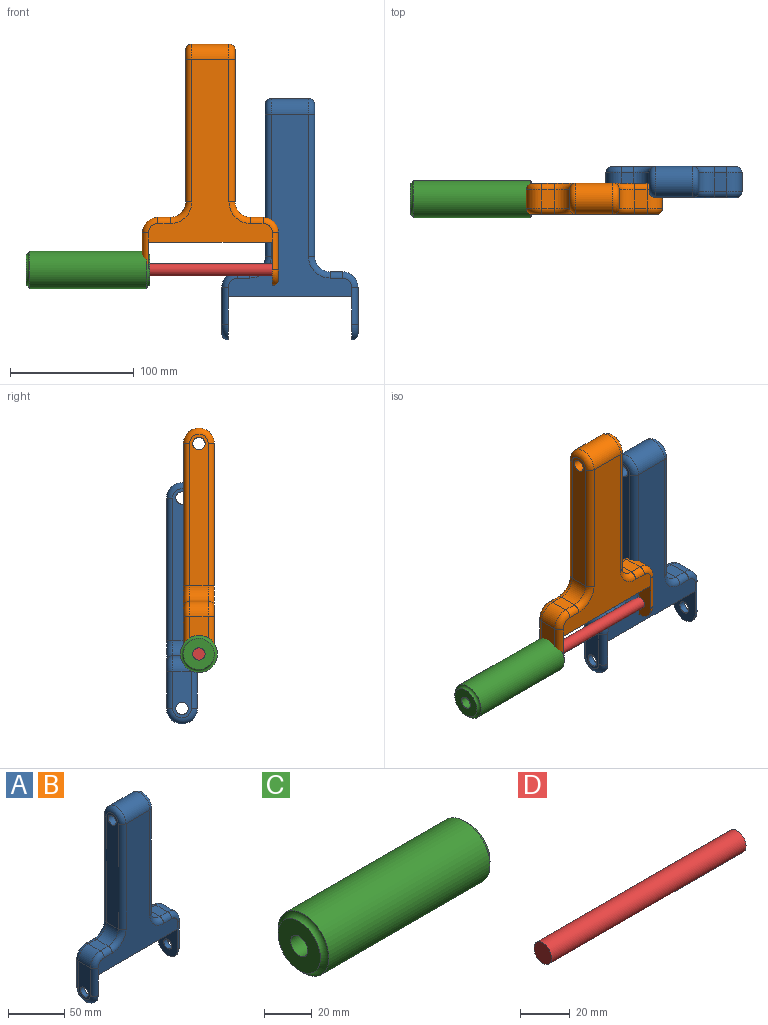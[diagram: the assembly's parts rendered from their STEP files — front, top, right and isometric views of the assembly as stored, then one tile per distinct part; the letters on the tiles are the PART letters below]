
ASSEMBLY  parts=4 mates=2
PART A: 43 faces, bbox 112.1x27.1x197.1 mm
  f0: plane 122.5x15mm, normal (-1,0,0), area 1734.8mm2, adj f11,f28,f29,f31,f42
  f1: plane 15x10mm, normal (0,0,1), area 150mm2, adj f11,f14,f32,f35
  f2: plane 37.5x15mm, normal (-1,0,0), area 459.8mm2, adj f14,f36,f38,f39,f41
  f3: plane 35x25mm, normal (1,0,0), area 729.4mm2, adj f4,f36,f38,f39,f41
  f4: plane 100x25mm, normal (0,0,-1), area 2500mm2, adj f3,f5,f9,f10
  f5: plane 35x25mm, normal (-1,0,0), area 729.4mm2, adj f4,f24,f26,f27,f40
  f6: plane 37.5x15mm, normal (1,0,0), area 459.8mm2, adj f13,f24,f26,f27,f40
  f7: plane 15x10mm, normal (0,0,1), area 150mm2, adj f12,f13,f20,f23
  f8: plane 122.5x15mm, normal (1,0,0), area 1734.8mm2, adj f12,f16,f17,f19,f42
  f9: plane 147.5x100mm, normal (0,-1,0), area 5582.3mm2, adj f4,f15,f19,f21,f23,f25,f27,f31
  f10: plane 147.5x100mm, normal (0,1,0), area 5582.3mm2, adj f4,f15,f16,f18,f20,f22,f24,f28
  f11: cylinder r=12.5mm len=15mm, axis (0,1,0), area 294.5mm2, adj f0,f1,f30,f33
  f12: cylinder r=12.5mm len=15mm, axis (0,-1,0), area 294.5mm2, adj f7,f8,f18,f21
  f13: cylinder r=12.5mm len=15mm, axis (0,1,0), area 294.5mm2, adj f6,f7,f22,f25
  f14: cylinder r=12.5mm len=15mm, axis (0,-1,0), area 294.5mm2, adj f1,f2,f34,f37
  f15: cylinder r=12.5mm len=30mm, axis (1,0,0), area 1178.1mm2, adj f9,f10,f17,f29
  f16: cylinder r=5mm len=115mm, axis (0,0,1), area 903.2mm2, adj f8,f10,f17,f18
  f17: torus R=7.5mm, axis (1,0,0), area 263.6mm2, adj f8,f15,f16,f19
  f18: torus R=17.5mm, axis (0,-1,0), area 176.6mm2, adj f10,f12,f16,f20
  f19: cylinder r=5mm len=115mm, axis (0,0,-1), area 903.2mm2, adj f8,f9,f17,f21
  f20: cylinder r=5mm len=10mm, axis (-1,0,0), area 78.5mm2, adj f7,f10,f18,f22
  f21: torus R=17.5mm, axis (0,-1,0), area 176.6mm2, adj f9,f12,f19,f23
  f22: torus R=7.5mm, axis (0,-1,0), area 131.8mm2, adj f10,f13,f20,f24
  f23: cylinder r=5mm len=10mm, axis (1,0,0), area 78.5mm2, adj f7,f9,f21,f25
  f24: cylinder r=5mm len=30mm, axis (0,0,1), area 235.6mm2, adj f5,f6,f10,f22,f26
  f25: torus R=7.5mm, axis (0,-1,0), area 131.8mm2, adj f9,f13,f23,f27
  f26: torus R=7.5mm, axis (1,0,0), area 263.6mm2, adj f5,f6,f24,f27
  f27: cylinder r=5mm len=30mm, axis (0,0,-1), area 235.6mm2, adj f5,f6,f9,f25,f26
  f28: cylinder r=5mm len=115mm, axis (0,0,-1), area 903.2mm2, adj f0,f10,f29,f30
  f29: torus R=7.5mm, axis (1,0,0), area 263.6mm2, adj f0,f15,f28,f31
  f30: torus R=17.5mm, axis (0,-1,0), area 176.6mm2, adj f10,f11,f28,f32
  f31: cylinder r=5mm len=115mm, axis (0,0,1), area 903.2mm2, adj f0,f9,f29,f33
  f32: cylinder r=5mm len=10mm, axis (-1,0,0), area 78.5mm2, adj f1,f10,f30,f34
  f33: torus R=17.5mm, axis (0,-1,0), area 176.6mm2, adj f9,f11,f31,f35
  f34: torus R=7.5mm, axis (0,-1,0), area 131.8mm2, adj f10,f14,f32,f36
  f35: cylinder r=5mm len=10mm, axis (1,0,0), area 78.5mm2, adj f1,f9,f33,f37
  f36: cylinder r=5mm len=30mm, axis (0,0,-1), area 235.6mm2, adj f2,f3,f10,f34,f38
  f37: torus R=7.5mm, axis (0,-1,0), area 131.8mm2, adj f9,f14,f35,f39
  f38: torus R=7.5mm, axis (1,0,0), area 263.6mm2, adj f2,f3,f36,f39
  f39: cylinder r=5mm len=30mm, axis (0,0,1), area 235.6mm2, adj f2,f3,f9,f37,f38
  f40: cylinder r=5mm len=10mm, axis (1,0,0), area 157.1mm2, adj f5,f6
  f41: cylinder r=5mm len=10mm, axis (1,0,0), area 157.1mm2, adj f2,f3
  f42: cylinder r=5mm len=40mm, axis (-1,0,0), area 1256.6mm2, adj f0,f8
PART B: same geometry as A
PART C: 6 faces, bbox 101.8x36.3x36.3 mm
  f0: plane 25x25mm, normal (1,0,0), area 412.3mm2, adj f1,f5
  f1: torus R=15mm, axis (-1,0,0), area 330.8mm2, adj f0,f2
  f2: cylinder r=15mm len=95mm, axis (-1,0,0), area 8953.5mm2, adj f1,f3
  f3: torus R=15mm, axis (-1,0,0), area 330.8mm2, adj f2,f4
  f4: plane 25x25mm, normal (-1,0,0), area 412.3mm2, adj f3,f5
  f5: cylinder r=5mm len=100mm, axis (1,0,0), area 3141.6mm2, adj f0,f4
PART D: 3 faces, bbox 110x10x10 mm
  f0: cylinder r=5mm len=110mm, axis (-1,0,0), area 3455.8mm2, adj f1,f2
  f1: plane 10x10mm, normal (1,0,0), area 78.5mm2, adj f0
  f2: plane 10x10mm, normal (-1,0,0), area 78.5mm2, adj f0
PLACE A t=(70.36,10.34,-10.25)mm
PLACE B t=(6.13,-3.31,33.79)mm fixed
PLACE C rot(axis=(-1,0,0),178.1deg) t=(-122.87,-15.33,-163.7)mm
PLACE D rot(axis=(0,1,0),180deg) t=(81.13,-15.81,-148.71)mm
MATE revolute C.f1 <-> B.f26  axis (1,0,0) through (-22.87,-15.81,-148.71)mm
MATE revolute B.f26 <-> D.f0  axis (1,0,0) through (-23.87,-15.81,-148.71)mm
